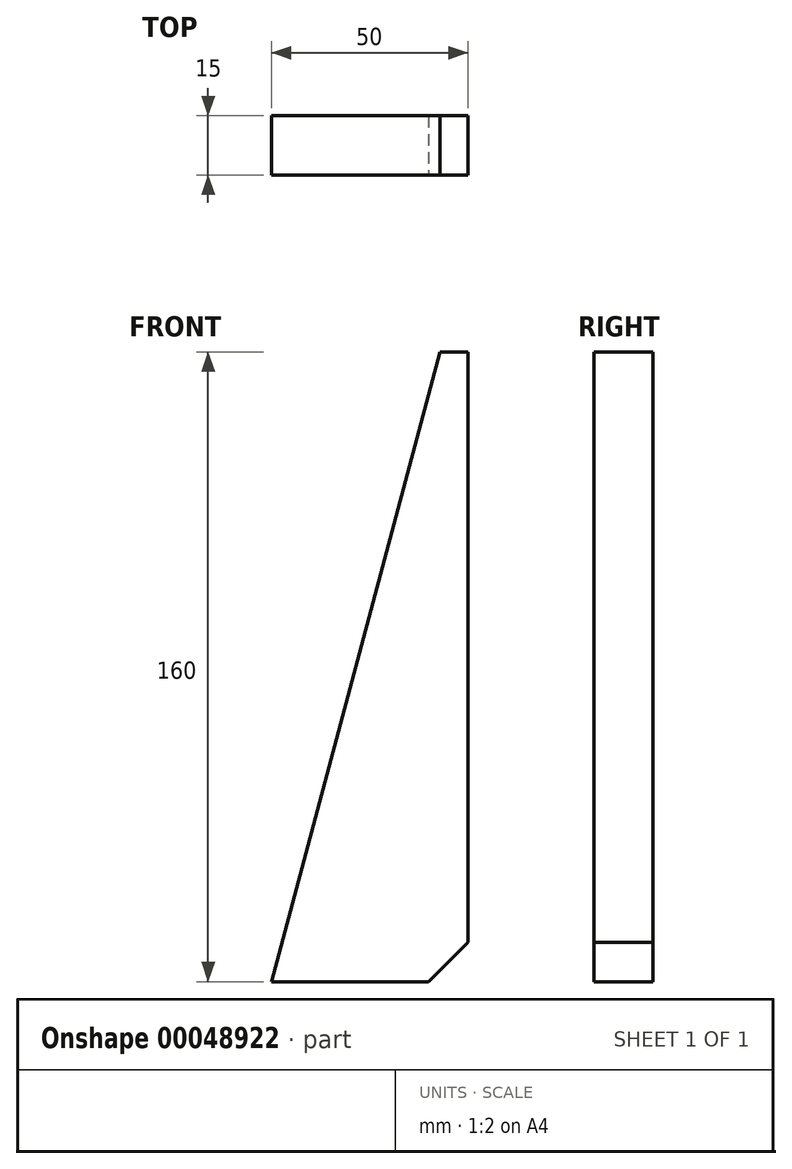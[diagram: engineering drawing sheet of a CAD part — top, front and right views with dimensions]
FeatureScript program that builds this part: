
annotation { "Feature Type Name" : "Feature", "Feature Type Description" : "" }
export const myFeature = defineFeature(function(context is Context, id is Id, definition is map)
    precondition{}
    {
        {
            var Q0;
            Q0=qCreatedBy(makeId("Front.planeOp"),FACE);
            var sketch = newSketch(context, id + "F0", { "sketchPlane" : qUnion([Q0])});
            skLineSegment(sketch, "E0.rect.bottom", {"start": v(25, 80) * mm, "end": v(-25, 80) * mm, "construction": true});
            skLineSegment(sketch, "E0.rect.top", {"start": v(25, -80) * mm, "end": v(-25, -80) * mm, "construction": true});
            skLineSegment(sketch, "E0.rect.left", {"start": v(25, 80) * mm, "end": v(25, -80) * mm, "construction": true});
            skLineSegment(sketch, "E0.rect.right", {"start": v(-25, 80) * mm, "end": v(-25, -80) * mm, "construction": true});
            skPoint(sketch, "E0.rect.middle", {"position": v(0, 0) * mm});
            skLineSegment(sketch, "E1", {"start": v(-25, -80) * mm, "end": v(17.87, 80) * mm});
            skLineSegment(sketch, "E2", {"start": v(-25, -80) * mm, "end": v(25, -80) * mm});
            skLineSegment(sketch, "E3", {"start": v(25, -80) * mm, "end": v(25, 80) * mm});
            skLineSegment(sketch, "E4", {"start": v(17.87, 80) * mm, "end": v(25, 80) * mm});
            skSolve(sketch);
        }
        {
            var Q0;
            Q0=makeQuery(id+"F0.imprint","IMPRINT",FACE,{"disambiguationData":[TD([[makeQuery(id+"F0.imprint","IMPRINT",EDGE,{"derivedFrom":sQuery(id+"F0.wireOp",EDGE,"E1")}),-1.0]])]});
            extrude(context, id + "F1", {"entities" : qUnion([Q0]), "depth" : 15 * mm});
        }
        {
            var Q0;
            Q0=makeQuery(id+"F1.opExtrude","SWEPT_EDGE",EDGE,{"disambiguationData":[OSD([sQuery(id+"F0.wireOp",EDGE,"E2"),sQuery(id+"F0.wireOp",EDGE,"E3")])]});
            chamfer(context, id + "F2", {"entities" : qUnion([Q0]), "width" : 10 * mm, "tangentPropagation" : true});
        }
    });
